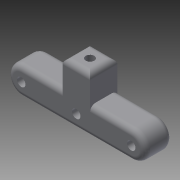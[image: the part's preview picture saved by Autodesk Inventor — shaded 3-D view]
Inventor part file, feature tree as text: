
AUTODESK INVENTOR PART (.ipt)
format: ipt  version: 2015 (Build 190159000, 159)  size: 151,040 bytes
history: native  units: mm
features: sketch x5, hole x3, extrude x2, fillet x1
ambient origin geometry x8: Origin, YZ Plane, XZ Plane, XY Plane, X Axis, Y Axis, Z Axis, Center Point
bodies: Solid1 (feature_tree)
feature tree (11):
  extrude  "Extrusion1"  Depth=10.0mm TaperAngle=0.0deg
  hole  "Hole1"  [1 undecoded]
  hole  "Hole2"  [1 undecoded]
  extrude  "Extrusion2"  [1 undecoded]
  fillet  "Fillet1"  [1 undecoded]
  hole  "Hole3"  [1 undecoded]
  sketch  "Sketch1"  dims[d2=40.0mm d3=10.0mm d4=0.0mm]
  sketch  "Sketch2"  dims[d5=3.1mm d6=6.0mm d7=4.0mm d8=5.0mm d9=90.0deg d10=8.0mm d11=20.594885mm]
  sketch  "Sketch3"  dims[d12=3.1mm d13=6.0mm d14=4.0mm d15=5.0mm d16=90.0deg d17=8.0mm d18=20.594885mm d19=10.0mm]
  sketch  "Sketch4"  dims[d20=5.0mm d21=10.0mm d22=0.0mm]
  sketch  "Sketch5"  dims[d23=2.0mm d24=3.1mm d25=6.0mm d26=4.0mm d27=5.0mm d28=90.0deg d29=8.0mm d30=0.0mm]
note: 5 required parameter values undecoded (feature->parameter linkage not recoverable at this tier; creation-order binding heuristic only, values carry confidence <= 0.55)
